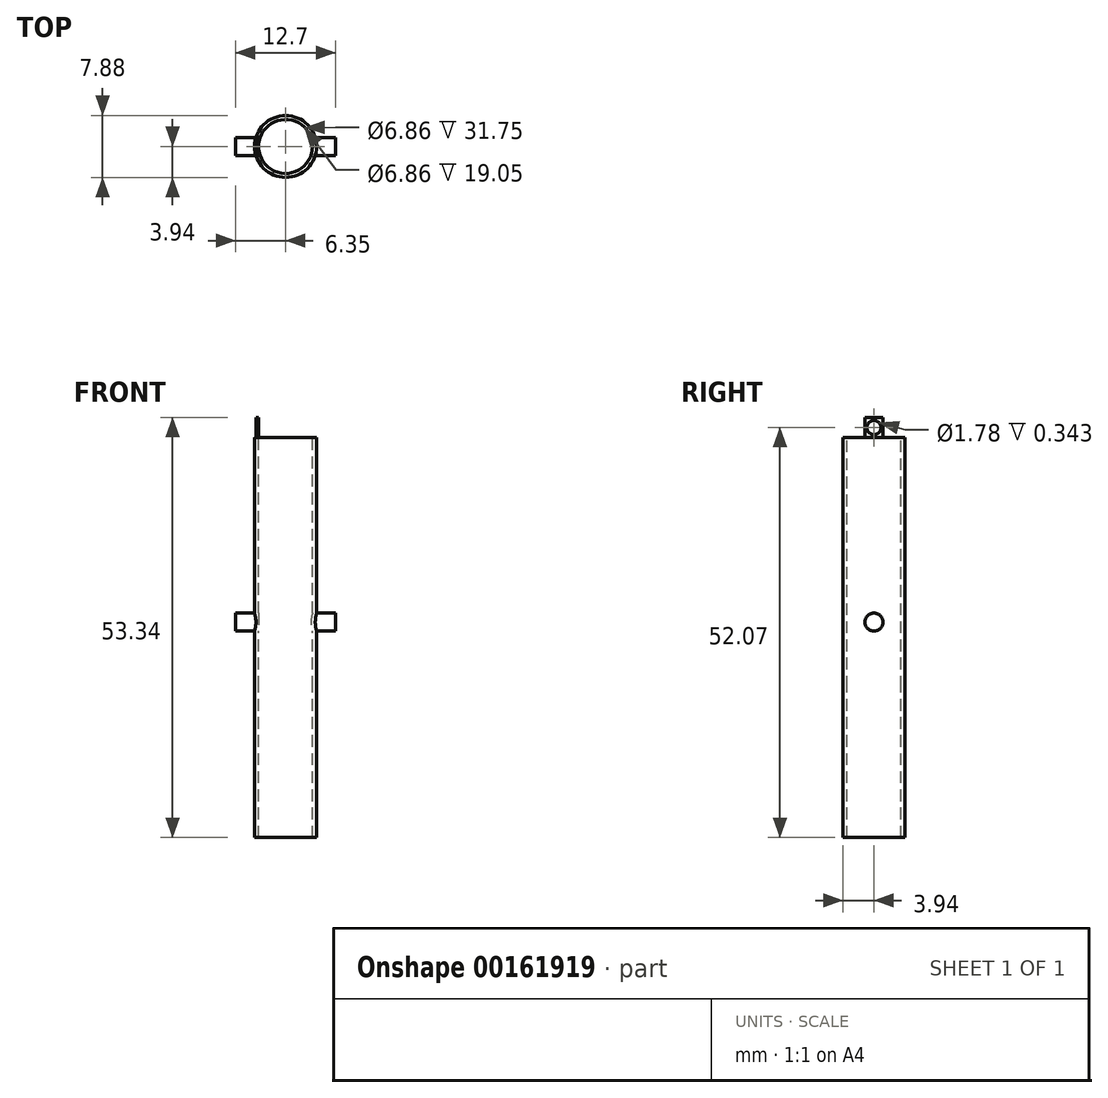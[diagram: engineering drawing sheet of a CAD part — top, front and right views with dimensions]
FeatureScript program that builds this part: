
annotation { "Feature Type Name" : "Feature", "Feature Type Description" : "" }
export const myFeature = defineFeature(function(context is Context, id is Id, definition is map)
    precondition{}
    {
        {
            var Q0;
            Q0=qCreatedBy(makeId("Top.planeOp"),FACE);
            var sketch = newSketch(context, id + "F0", { "sketchPlane" : qUnion([Q0])});
            skCircle(sketch, "E0", {"center": v(0, 0) * mm, "radius": 3.94 * mm});
            skSolve(sketch);
        }
        {
            var Q0;
            Q0=makeQuery(id+"F0.imprint","IMPRINT",FACE,{"disambiguationData":[TD([[makeQuery(id+"F0.imprint","IMPRINT",EDGE,{"derivedFrom":sQuery(id+"F0.wireOp",EDGE,"E0")}),1.0]])]});
            extrude(context, id + "F1", {"entities" : qUnion([Q0]), "depth" : 31.75 * mm});
        }
        {
            var Q0;
            Q0=makeQuery(id+"F1.opExtrude","CAP_FACE",FACE,{"disambiguationData":[OSD([sQuery(id+"F0.wireOp",EDGE,"E0")])],"isStart":false});
            var sketch = newSketch(context, id + "F2", { "sketchPlane" : qUnion([Q0])});
            skCircle(sketch, "E1", {"center": v(0, 0) * mm, "radius": 3.43 * mm});
            skSolve(sketch);
        }
        {
            var Q0;
            Q0=makeQuery(id+"F2.imprint","IMPRINT",FACE,{"disambiguationData":[TD([[makeQuery(id+"F2.imprint","IMPRINT",EDGE,{"derivedFrom":sQuery(id+"F2.wireOp",EDGE,"E1")}),1.0]])]});
            extrude(context, id + "F3", {"entities" : qUnion([Q0]), "operationType" : NewBodyOperationType.REMOVE, "oppositeDirection" : true, "depth" : 31.75 * mm});
        }
        {
            var Q0;
            Q0=qCreatedBy(makeId("Right.planeOp"),FACE);
            var sketch = newSketch(context, id + "F4", { "sketchPlane" : qUnion([Q0])});
            skLineSegment(sketch, "E2", {"start": v(0, 0) * mm, "end": v(0, 8.3) * mm});
            skCircle(sketch, "E3", {"center": v(0, 8.3) * mm, "radius": 1.14 * mm});
            skSolve(sketch);
        }
        {
            var Q0;
            Q0=makeQuery(id+"F4.imprint","IMPRINT",FACE,{"disambiguationData":[TD([[makeQuery(id+"F4.imprint","IMPRINT",EDGE,{"derivedFrom":sQuery(id+"F4.wireOp",EDGE,"E3")}),1.0]])]});
            extrude(context, id + "F5", {"entities" : qUnion([Q0]), "operationType" : NewBodyOperationType.ADD, "depth" : 6.35 * mm});
        }
        {
            var Q0;
            Q0=makeQuery(id+"F5.opExtrude","CAP_FACE",FACE,{"disambiguationData":[OSD([sQuery(id+"F4.wireOp",EDGE,"E3")])],"isStart":true});
            extrude(context, id + "F6", {"entities" : qUnion([Q0]), "operationType" : NewBodyOperationType.ADD, "depth" : 6.35 * mm});
        }
        {
            var Q0;
            Q0=makeQuery(id+"F1.opExtrude","CAP_FACE",FACE,{"disambiguationData":[OSD([sQuery(id+"F0.wireOp",EDGE,"E0")])],"isStart":true});
            var sketch = newSketch(context, id + "F7", { "sketchPlane" : qUnion([Q0])});
            skCircle(sketch, "E4", {"center": v(0, 0) * mm, "radius": 3.43 * mm});
            skSolve(sketch);
        }
        {
            var Q0;
            Q0=makeQuery(id+"F7.imprint","IMPRINT",FACE,{"disambiguationData":[TD([[makeQuery(id+"F7.imprint","IMPRINT",EDGE,{"derivedFrom":sQuery(id+"F7.wireOp",EDGE,"E4")}),1.0]])]});
            extrude(context, id + "F8", {"entities" : qUnion([Q0]), "operationType" : NewBodyOperationType.REMOVE, "oppositeDirection" : true, "depth" : 31.75 * mm});
        }
        {
            var Q0;
            Q0=makeQuery(id+"F1.opExtrude","CAP_FACE",FACE,{"disambiguationData":[OSD([sQuery(id+"F0.wireOp",EDGE,"E0")])],"isStart":true});
            extrude(context, id + "F9", {"entities" : qUnion([Q0]), "operationType" : NewBodyOperationType.ADD, "depth" : 19.05 * mm});
        }
        {
            var Q0;
            Q0=makeQuery(id+"F1.opExtrude","CAP_FACE",FACE,{"disambiguationData":[OSD([sQuery(id+"F0.wireOp",EDGE,"E0")])],"isStart":false});
            var sketch = newSketch(context, id + "F10", { "sketchPlane" : qUnion([Q0])});
            skLineSegment(sketch, "E5.bottom", {"start": v(-3.77, -1.15) * mm, "end": v(-3.42, -1.15) * mm});
            skLineSegment(sketch, "E5.top", {"start": v(-3.77, 1.12) * mm, "end": v(-3.42, 1.12) * mm});
            skLineSegment(sketch, "E5.left", {"start": v(-3.77, -1.15) * mm, "end": v(-3.77, 1.12) * mm});
            skLineSegment(sketch, "E5.right", {"start": v(-3.42, -1.15) * mm, "end": v(-3.42, 1.12) * mm});
            skSolve(sketch);
        }
        {
            var Q0;
            {var subQ1=sQuery(id+"F10.wireOp",EDGE,"E5.bottom");Q0=makeQuery(id+"F10.imprint","IMPRINT",FACE,{"disambiguationData":[TD([[makeQuery(id+"F10.imprint","IMPRINT",EDGE,{"derivedFrom":subQ1}),1.0]])]});}
            extrude(context, id + "F11", {"entities" : qUnion([Q0]), "operationType" : NewBodyOperationType.ADD, "depth" : 2.54 * mm});
        }
        {
            var Q0;
            Q0=makeQuery(id+"F11.opExtrude","SWEPT_FACE",FACE,{"disambiguationData":[OSD([sQuery(id+"F10.wireOp",EDGE,"E5.left")])]});
            var sketch = newSketch(context, id + "F12", { "sketchPlane" : qUnion([Q0])});
            skLineSegment(sketch, "E6", {"start": v(0, 34.3) * mm, "end": v(0, 31.75) * mm});
            skCircle(sketch, "E7", {"center": v(0, 33.02) * mm, "radius": 0.89 * mm});
            skSolve(sketch);
        }
        {
            var Q0;
            {var subQ0=sQuery(id+"F12.wireOp",EDGE,"E7");var subQ1=sQuery(id+"F12.wireOp",EDGE,"E6");var subQ2=makeQuery(id+"F12.imprint","INTERSECT",VERTEX,{"disambiguationData":[OD(0.0)],"derivedFrom":[subQ1,subQ0]});Q0=makeQuery(id+"F12.imprint","IMPRINT",FACE,{"disambiguationData":[TD([[makeQuery(id+"F12.imprint","IMPRINT",EDGE,{"disambiguationData":[TD([[subQ2,-1.0]])],"derivedFrom":subQ1}),-1.0]])]});}
            var Q1;
            {var subQ0=sQuery(id+"F12.wireOp",EDGE,"E7");var subQ1=sQuery(id+"F12.wireOp",EDGE,"E6");var subQ2=makeQuery(id+"F12.imprint","INTERSECT",VERTEX,{"disambiguationData":[OD(0.0)],"derivedFrom":[subQ1,subQ0]});Q1=makeQuery(id+"F12.imprint","IMPRINT",FACE,{"disambiguationData":[TD([[makeQuery(id+"F12.imprint","IMPRINT",EDGE,{"disambiguationData":[TD([[subQ2,-1.0]])],"derivedFrom":subQ1}),1.0]])]});}
            extrude(context, id + "F13", {"entities" : qUnion([Q0, Q1]), "operationType" : NewBodyOperationType.REMOVE, "oppositeDirection" : true, "depth" : 25.4 * mm});
        }
    });
